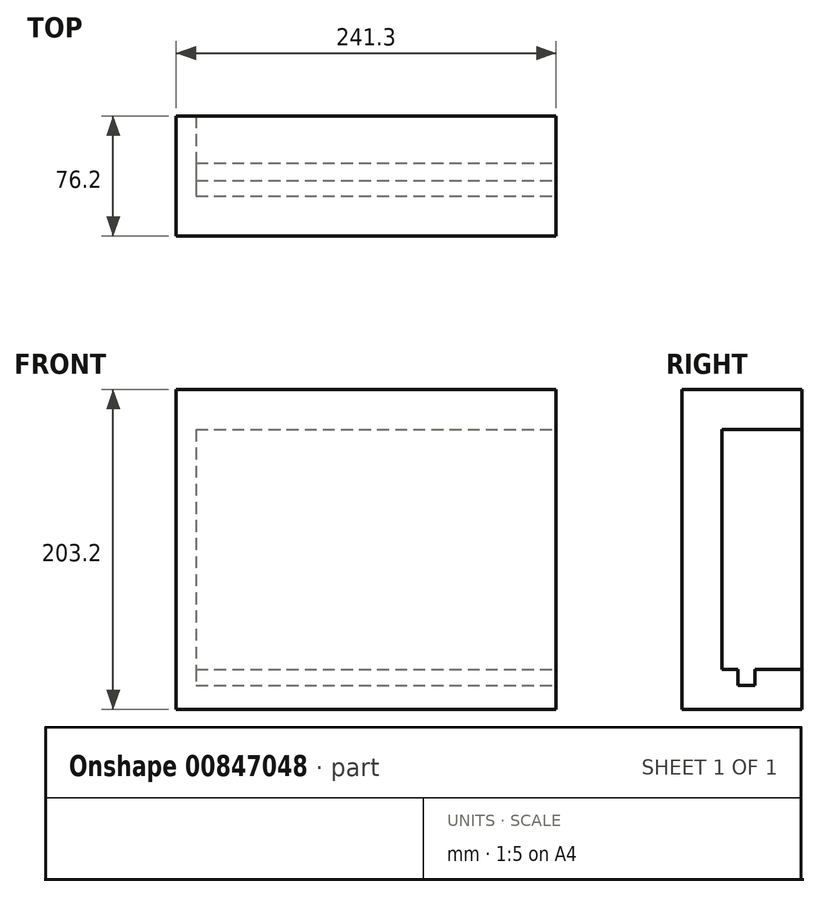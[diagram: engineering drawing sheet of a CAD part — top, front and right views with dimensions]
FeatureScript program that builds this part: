
annotation { "Feature Type Name" : "Feature", "Feature Type Description" : "" }
export const myFeature = defineFeature(function(context is Context, id is Id, definition is map)
    precondition{}
    {
        {
            var Q0;
            Q0=qCreatedBy(makeId("Top.planeOp"),FACE);
            var sketch = newSketch(context, id + "F0", { "sketchPlane" : qUnion([Q0])});
            skLineSegment(sketch, "E0.right", {"start": v(97.44, -125.76) * mm, "end": v(97.44, 52.04) * mm});
            skLineSegment(sketch, "E1.bottom", {"start": v(-131.16, 26.64) * mm, "end": v(97.44, 26.64) * mm});
            skLineSegment(sketch, "E1.top", {"start": v(-131.16, -24.16) * mm, "end": v(97.44, -24.16) * mm});
            skLineSegment(sketch, "E1.left", {"start": v(-131.16, 26.64) * mm, "end": v(-131.16, -24.16) * mm});
            skLineSegment(sketch, "E1.right", {"start": v(97.44, 26.64) * mm, "end": v(97.44, -24.16) * mm});
            skLineSegment(sketch, "E2.right", {"start": v(97.44, -49.56) * mm, "end": v(97.44, -100.36) * mm});
            skLineSegment(sketch, "E3.right", {"start": v(97.44, -80.36) * mm, "end": v(97.44, -90.36) * mm});
            skLineSegment(sketch, "E4.bottom", {"start": v(-131.16, -14.16) * mm, "end": v(97.44, -14.16) * mm});
            skLineSegment(sketch, "E4.top", {"start": v(-131.16, -3.16) * mm, "end": v(97.44, -3.16) * mm});
            skLineSegment(sketch, "E4.left", {"start": v(-131.16, -14.16) * mm, "end": v(-131.16, -3.16) * mm});
            skLineSegment(sketch, "E4.right", {"start": v(97.44, -14.16) * mm, "end": v(97.44, -3.16) * mm});
            skLineSegment(sketch, "E5.top", {"start": v(-143.86, -49.56) * mm, "end": v(97.44, -49.56) * mm});
            skLineSegment(sketch, "E5.right", {"start": v(97.44, 64.74) * mm, "end": v(97.44, -49.56) * mm});
            skLineSegment(sketch, "E6", {"start": v(-131.16, 26.64) * mm, "end": v(-143.86, 26.64) * mm});
            skLineSegment(sketch, "E7", {"start": v(-143.86, 26.64) * mm, "end": v(-143.86, -49.56) * mm});
            skSolve(sketch);
        }
        {
            var Q0;
            {var subQ0=sQuery(id+"F0.wireOp",EDGE,"E0.bottom");Q0=makeQuery(id+"F0.imprint","IMPRINT",FACE,{"disambiguationData":[TD([[makeQuery(id+"F0.imprint","IMPRINT",EDGE,{"derivedFrom":subQ0}),1.0]])]});}
            var Q1;
            {var subQ0=sQuery(id+"F0.wireOp",EDGE,"E1.top");Q1=makeQuery(id+"F0.imprint","IMPRINT",FACE,{"disambiguationData":[TD([[makeQuery(id+"F0.imprint","IMPRINT",EDGE,{"derivedFrom":subQ0}),-1.0]])]});}
            var Q2;
            {var subQ0=sQuery(id+"F0.wireOp",EDGE,"E0.top");Q2=makeQuery(id+"F0.imprint","IMPRINT",FACE,{"disambiguationData":[TD([[makeQuery(id+"F0.imprint","IMPRINT",EDGE,{"derivedFrom":subQ0}),-1.0]])]});}
            extrude(context, id + "F1", {"entities" : qUnion([Q0, Q1, Q2]), "depth" : 203.2 * mm, "offsetDistance" : 25.4 * mm});
        }
        {
            var Q0;
            {var subQ0=sQuery(id+"F0.wireOp",EDGE,"E2.top");Q0=makeQuery(id+"F0.imprint","IMPRINT",FACE,{"disambiguationData":[TD([[makeQuery(id+"F0.imprint","IMPRINT",EDGE,{"derivedFrom":subQ0}),1.0]])]});}
            var Q1;
            {var subQ0=sQuery(id+"F0.wireOp",EDGE,"E2.bottom");Q1=makeQuery(id+"F0.imprint","IMPRINT",FACE,{"disambiguationData":[TD([[makeQuery(id+"F0.imprint","IMPRINT",EDGE,{"derivedFrom":subQ0}),-1.0]])]});}
            var Q2;
            {var subQ0=sQuery(id+"F0.wireOp",EDGE,"E1.top");Q2=makeQuery(id+"F0.imprint","IMPRINT",FACE,{"disambiguationData":[TD([[makeQuery(id+"F0.imprint","IMPRINT",EDGE,{"derivedFrom":subQ0}),1.0]])]});}
            var Q3;
            {var subQ0=sQuery(id+"F0.wireOp",EDGE,"E1.bottom");Q3=makeQuery(id+"F0.imprint","IMPRINT",FACE,{"disambiguationData":[TD([[makeQuery(id+"F0.imprint","IMPRINT",EDGE,{"derivedFrom":subQ0}),-1.0]])]});}
            extrude(context, id + "F2", {"entities" : qUnion([Q0, Q1, Q2, Q3]), "depth" : 25.4 * mm, "offsetDistance" : 25.4 * mm});
        }
        {
            var Q0;
            Q0=makeQuery(id+"F0.imprint","IMPRINT",FACE,{"disambiguationData":[TD([[makeQuery(id+"F0.imprint","IMPRINT",EDGE,{"derivedFrom":sQuery(id+"F0.wireOp",EDGE,"E3.bottom")}),-1.0]])]});
            var Q1;
            Q1=makeQuery(id+"F0.imprint","IMPRINT",FACE,{"disambiguationData":[TD([[makeQuery(id+"F0.imprint","IMPRINT",EDGE,{"derivedFrom":sQuery(id+"F0.wireOp",EDGE,"E4.bottom")}),1.0]])]});
            extrude(context, id + "F3", {"entities" : qUnion([Q0, Q1]), "depth" : 15.24 * mm, "offsetDistance" : 25.4 * mm});
        }
        {
            var Q0;
            Q0=makeQuery(id+"F1.opExtrude","CAP_FACE",FACE,{"disambiguationData":[OSD([sQuery(id+"F0.wireOp",EDGE,"E1.top"),sQuery(id+"F0.wireOp",EDGE,"E1.left"),sQuery(id+"F0.wireOp",EDGE,"E4.left"),sQuery(id+"F0.wireOp",EDGE,"E5.top"),sQuery(id+"F0.wireOp",EDGE,"E5.right"),sQuery(id+"F0.wireOp",EDGE,"E6"),sQuery(id+"F0.wireOp",EDGE,"E7")])],"isStart":false});
            var sketch = newSketch(context, id + "F4", { "sketchPlane" : qUnion([Q0])});
            skLineSegment(sketch, "E8.bottom", {"start": v(97.44, -49.56) * mm, "end": v(-143.86, -49.56) * mm});
            skLineSegment(sketch, "E8.top", {"start": v(97.44, 26.64) * mm, "end": v(-143.86, 26.64) * mm});
            skLineSegment(sketch, "E8.left", {"start": v(97.44, -49.56) * mm, "end": v(97.44, 26.64) * mm});
            skLineSegment(sketch, "E8.right", {"start": v(-143.86, -49.56) * mm, "end": v(-143.86, 26.64) * mm});
            skSolve(sketch);
        }
        {
            var Q0;
            {var subQ4=makeQuery(id+"F1.opExtrude","CAP_EDGE",EDGE,{"disambiguationData":[OSD([sQuery(id+"F0.wireOp",EDGE,"E1.top")])],"isStart":false});Q0=makeQuery(id+"F4.imprint","IMPRINT",FACE,{"disambiguationData":[TD([[makeQuery(id+"F4.imprint","IMPRINT",EDGE,{"derivedFrom":subQ4}),1.0]])]});}
            extrude(context, id + "F5", {"entities" : qUnion([Q0]), "operationType" : NewBodyOperationType.ADD, "oppositeDirection" : true, "depth" : 25.4 * mm, "offsetDistance" : 25.4 * mm});
        }
        {
            var Q0;
            Q0=makeQuery(id+"F5.boolean.opBoolean","MERGE",FACE,{"derivedFrom":[makeQuery(id+"F1.opExtrude","SWEPT_FACE",FACE,{"disambiguationData":[OSD([sQuery(id+"F0.wireOp",EDGE,"E5.right")])]}),makeQuery(id+"F5.opExtrude","SWEPT_FACE",FACE,{"disambiguationData":[OSD([sQuery(id+"F4.wireOp",EDGE,"E8.left")])]})]});
            var sketch = newSketch(context, id + "F6", { "sketchPlane" : qUnion([Q0])});
            skLineSegment(sketch, "E9.bottom", {"start": v(-49.56, 0) * mm, "end": v(-16.4, 0) * mm});
            skLineSegment(sketch, "E9.top", {"start": v(-49.56, 23.35) * mm, "end": v(-16.4, 23.35) * mm});
            skLineSegment(sketch, "E9.left", {"start": v(-49.56, 0) * mm, "end": v(-49.56, 23.35) * mm});
            skLineSegment(sketch, "E9.right", {"start": v(-16.4, 0) * mm, "end": v(-16.4, 23.35) * mm});
            skSolve(sketch);
        }
        {
            var Q0;
            Q0=qSketchRegion(id+"F6",true);
            extrude(context, id + "F7", {"entities" : qUnion([Q0]), "operationType" : NewBodyOperationType.ADD, "oppositeDirection" : true, "depth" : 25.4 * mm, "offsetDistance" : 25.4 * mm});
        }
        {
            var Q0;
            Q0=makeQuery(id+"F2.opExtrude","CAP_FACE",FACE,{"disambiguationData":[OSD([sQuery(id+"F0.wireOp",EDGE,"E1.bottom"),sQuery(id+"F0.wireOp",EDGE,"E1.left"),sQuery(id+"F0.wireOp",EDGE,"E4.top"),sQuery(id+"F0.wireOp",EDGE,"E5.right")])],"isStart":true});
            var sketch = newSketch(context, id + "F8", { "sketchPlane" : qUnion([Q0])});
            skLineSegment(sketch, "E10.bottom", {"start": v(97.44, -26.64) * mm, "end": v(-133.7, -26.64) * mm});
            skLineSegment(sketch, "E10.top", {"start": v(97.44, 33.38) * mm, "end": v(-133.7, 33.38) * mm});
            skLineSegment(sketch, "E10.left", {"start": v(97.44, -26.64) * mm, "end": v(97.44, 33.38) * mm});
            skLineSegment(sketch, "E10.right", {"start": v(-133.7, -26.64) * mm, "end": v(-133.7, 33.38) * mm});
            skSolve(sketch);
        }
        {
            var Q0;
            Q0=qSketchRegion(id+"F8",true);
            extrude(context, id + "F9", {"entities" : qUnion([Q0]), "operationType" : NewBodyOperationType.ADD, "oppositeDirection" : true, "depth" : 0.25 * mm, "offsetDistance" : 25.4 * mm});
        }
    });
